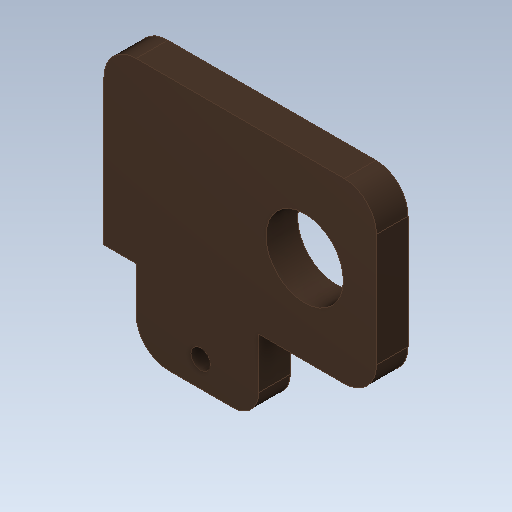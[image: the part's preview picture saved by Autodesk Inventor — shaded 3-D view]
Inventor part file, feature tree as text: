
AUTODESK INVENTOR PART (.ipt)
format: ipt  version: 2020 (Build 240168000, 168)  size: 119,296 bytes
history: native  units: mm
features: other x1, extrude x1, sketch x1
ambient origin geometry x8: Origin, YZ Plane, XZ Plane, XY Plane, X Axis, Y Axis, Z Axis, Center Point
bodies: Body1 (feature_tree)
feature tree (3):
  other  "Твердое тело1"
  extrude  "Выдавливание1"  Depth=4.9mm TaperAngle=0.0deg
  sketch  "Эскиз1"
